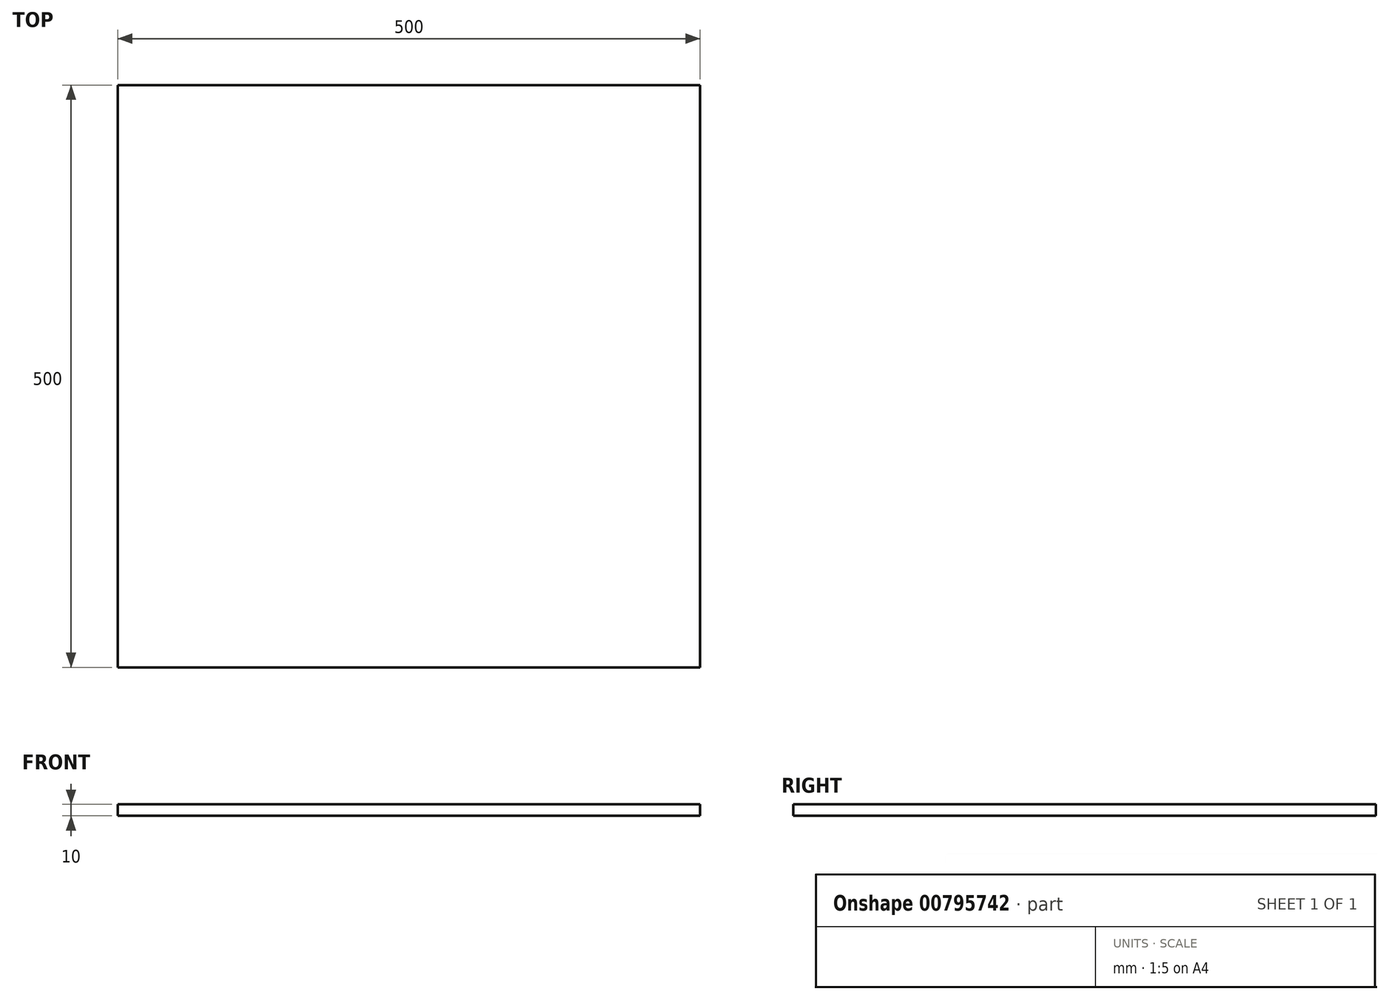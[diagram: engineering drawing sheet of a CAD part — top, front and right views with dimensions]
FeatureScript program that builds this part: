
annotation { "Feature Type Name" : "Feature", "Feature Type Description" : "" }
export const myFeature = defineFeature(function(context is Context, id is Id, definition is map)
    precondition{}
    {
        {
            var Q0;
            Q0=qCreatedBy(makeId("Top.planeOp"),FACE);
            var sketch = newSketch(context, id + "F0", { "sketchPlane" : qUnion([Q0])});
            skLineSegment(sketch, "E0.bottom", {"start": v(250, -250) * mm, "end": v(-250, -250) * mm});
            skLineSegment(sketch, "E0.top", {"start": v(250, 250) * mm, "end": v(-250, 250) * mm});
            skLineSegment(sketch, "E0.left", {"start": v(250, -250) * mm, "end": v(250, 250) * mm});
            skLineSegment(sketch, "E0.right", {"start": v(-250, -250) * mm, "end": v(-250, 250) * mm});
            skPoint(sketch, "E0.middle", {"position": v(0, 0) * mm});
            skSolve(sketch);
        }
        {
            var Q0;
            Q0=makeQuery(id+"F0.imprint","IMPRINT",FACE,{"disambiguationData":[TD([[makeQuery(id+"F0.imprint","IMPRINT",EDGE,{"derivedFrom":sQuery(id+"F0.wireOp",EDGE,"E0.bottom")}),-1.0]])]});
            extrude(context, id + "F1", {"entities" : qUnion([Q0]), "depth" : 10 * mm, "offsetDistance" : 25 * mm});
        }
    });
